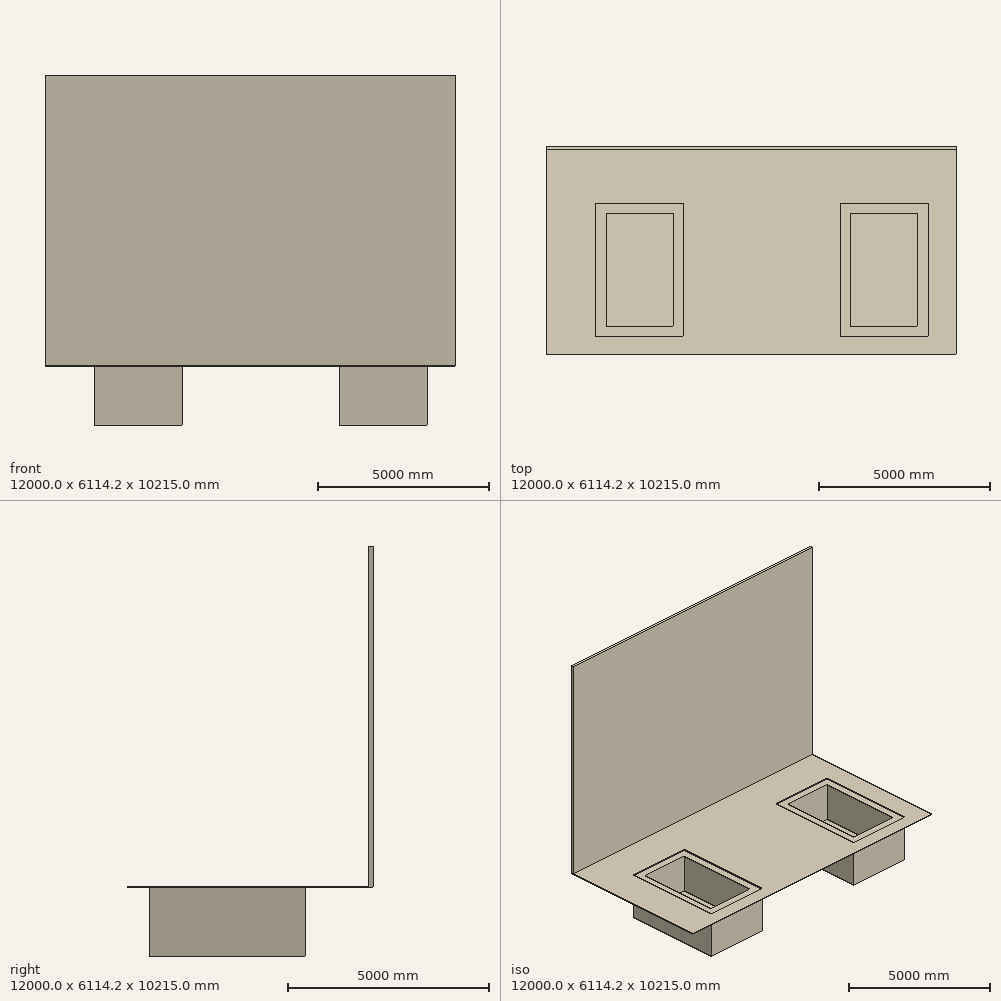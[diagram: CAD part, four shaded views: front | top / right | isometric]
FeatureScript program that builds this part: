
annotation { "Feature Type Name" : "Feature", "Feature Type Description" : "" }
export const myFeature = defineFeature(function(context is Context, id is Id, definition is map)
    precondition{}
    {
        {
            var Q0;
            Q0=qCreatedBy(makeId("Top.planeOp"),FACE);
            var sketch = newSketch(context, id + "F0", { "sketchPlane" : qUnion([Q0])});
            skLineSegment(sketch, "E0.bottom", {"start": v(-6000, -2994.9) * mm, "end": v(6000, -2994.9) * mm});
            skLineSegment(sketch, "E0.top", {"start": v(-6000, 3005.1) * mm, "end": v(6000, 3005.1) * mm});
            skLineSegment(sketch, "E0.left", {"start": v(-6000, -2994.9) * mm, "end": v(-6000, 3005.1) * mm});
            skLineSegment(sketch, "E0.right", {"start": v(6000, -2994.9) * mm, "end": v(6000, 3005.1) * mm});
            skPoint(sketch, "E0.middle", {"position": v(0, 5.1) * mm});
            skLineSegment(sketch, "E1.top", {"start": v(-6000, 3119.27) * mm, "end": v(6000, 3119.27) * mm});
            skLineSegment(sketch, "E1.left", {"start": v(-6000, 3005.1) * mm, "end": v(-6000, 3119.27) * mm});
            skLineSegment(sketch, "E1.right", {"start": v(6000, 3005.1) * mm, "end": v(6000, 3119.27) * mm});
            skLineSegment(sketch, "E2.bottom", {"start": v(-4253.15, 1135.1) * mm, "end": v(-2293.15, 1135.1) * mm});
            skLineSegment(sketch, "E2.top", {"start": v(-4253.15, -2164.9) * mm, "end": v(-2293.15, -2164.9) * mm});
            skLineSegment(sketch, "E2.left", {"start": v(-4253.15, 1135.1) * mm, "end": v(-4253.15, -2164.9) * mm});
            skLineSegment(sketch, "E2.right", {"start": v(-2293.15, 1135.1) * mm, "end": v(-2293.15, -2164.9) * mm});
            skLineSegment(sketch, "E3.bottom", {"start": v(2906.85, 1135.1) * mm, "end": v(4866.85, 1135.1) * mm});
            skLineSegment(sketch, "E3.top", {"start": v(2906.85, -2164.9) * mm, "end": v(4866.85, -2164.9) * mm});
            skLineSegment(sketch, "E3.left", {"start": v(2906.85, 1135.1) * mm, "end": v(2906.85, -2164.9) * mm});
            skLineSegment(sketch, "E3.right", {"start": v(4866.85, 1135.1) * mm, "end": v(4866.85, -2164.9) * mm});
            skLineSegment(sketch, "E4.bottom", {"start": v(2606.85, 1435.1) * mm, "end": v(5166.85, 1435.1) * mm});
            skLineSegment(sketch, "E4.top", {"start": v(2606.85, -2464.9) * mm, "end": v(5166.85, -2464.9) * mm});
            skLineSegment(sketch, "E4.left", {"start": v(2606.85, 1435.1) * mm, "end": v(2606.85, -2464.9) * mm});
            skLineSegment(sketch, "E4.right", {"start": v(5166.85, 1435.1) * mm, "end": v(5166.85, -2464.9) * mm});
            skPoint(sketch, "E4.middle", {"position": v(3886.85, -514.9) * mm});
            skLineSegment(sketch, "E5.bottom", {"start": v(-4553.15, 1435.1) * mm, "end": v(-1993.15, 1435.1) * mm});
            skLineSegment(sketch, "E5.top", {"start": v(-4553.15, -2464.9) * mm, "end": v(-1993.15, -2464.9) * mm});
            skLineSegment(sketch, "E5.left", {"start": v(-4553.15, 1435.1) * mm, "end": v(-4553.15, -2464.9) * mm});
            skLineSegment(sketch, "E5.right", {"start": v(-1993.15, 1435.1) * mm, "end": v(-1993.15, -2464.9) * mm});
            skPoint(sketch, "E5.middle", {"position": v(-3273.15, -514.9) * mm});
            skSolve(sketch);
        }
        {
            var Q0;
            Q0=makeQuery(id+"F0.imprint","IMPRINT",FACE,{"disambiguationData":[TD([[makeQuery(id+"F0.imprint","IMPRINT",EDGE,{"derivedFrom":sQuery(id+"F0.wireOp",EDGE,"E0.top")}),1.0]])]});
            extrude(context, id + "F1", {"entities" : qUnion([Q0]), "depth" : 8500 * mm});
        }
        {
            var Q0;
            Q0 = qSketchRegion(id + "F0", true);
            extrude(context, id + "F2", {"entities" : qUnion([Q0]), "depth" : 25 * mm});
        }
        {
            var Q0;
            Q0=makeQuery(id+"F0.imprint","IMPRINT",FACE,{"disambiguationData":[TD([[makeQuery(id+"F0.imprint","IMPRINT",EDGE,{"derivedFrom":sQuery(id+"F0.wireOp",EDGE,"E2.bottom")}),-1.0]])]});
            var Q1;
            Q1=makeQuery(id+"F0.imprint","IMPRINT",FACE,{"disambiguationData":[TD([[makeQuery(id+"F0.imprint","IMPRINT",EDGE,{"derivedFrom":sQuery(id+"F0.wireOp",EDGE,"E2.bottom")}),1.0]])]});
            var Q2;
            Q2=makeQuery(id+"F0.imprint","IMPRINT",FACE,{"disambiguationData":[TD([[makeQuery(id+"F0.imprint","IMPRINT",EDGE,{"derivedFrom":sQuery(id+"F0.wireOp",EDGE,"E3.bottom")}),-1.0]])]});
            var Q3;
            Q3=makeQuery(id+"F0.imprint","IMPRINT",FACE,{"disambiguationData":[TD([[makeQuery(id+"F0.imprint","IMPRINT",EDGE,{"derivedFrom":sQuery(id+"F0.wireOp",EDGE,"E3.bottom")}),1.0]])]});
            extrude(context, id + "F3", {"entities" : qUnion([Q0, Q1, Q2, Q3]), "oppositeDirection" : true, "depth" : 1715 * mm});
        }
        {
            var Q0;
            Q0=makeQuery(id+"F3.opExtrude","CAP_FACE",FACE,{"disambiguationData":[OSD([sQuery(id+"F0.wireOp",EDGE,"E5.bottom"),sQuery(id+"F0.wireOp",EDGE,"E5.top"),sQuery(id+"F0.wireOp",EDGE,"E5.left"),sQuery(id+"F0.wireOp",EDGE,"E5.right")])],"isStart":true});
            var Q1;
            Q1=makeQuery(id+"F3.opExtrude","CAP_FACE",FACE,{"disambiguationData":[OSD([sQuery(id+"F0.wireOp",EDGE,"E4.bottom"),sQuery(id+"F0.wireOp",EDGE,"E4.top"),sQuery(id+"F0.wireOp",EDGE,"E4.left"),sQuery(id+"F0.wireOp",EDGE,"E4.right")])],"isStart":true});
            shell(context, id + "F4", {"entities" : qUnion([Q0, Q1]), "thickness" : 300 * mm});
        }
    });
